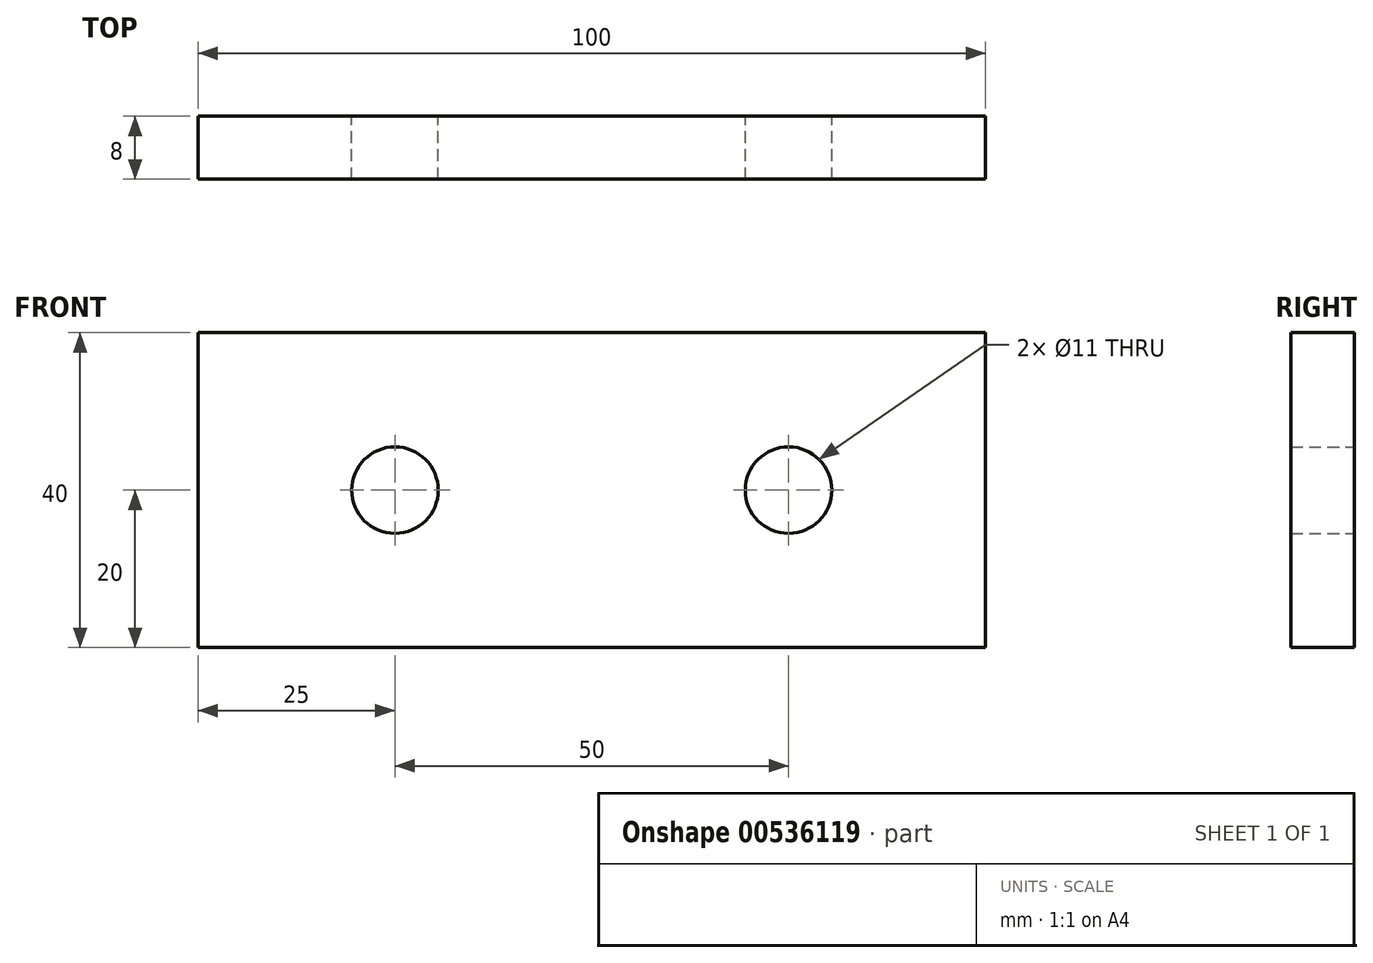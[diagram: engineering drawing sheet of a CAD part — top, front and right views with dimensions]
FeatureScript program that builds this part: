
annotation { "Feature Type Name" : "Feature", "Feature Type Description" : "" }
export const myFeature = defineFeature(function(context is Context, id is Id, definition is map)
    precondition{}
    {
        {
            var Q0;
            Q0=qCreatedBy(makeId("Front.planeOp"),FACE);
            var sketch = newSketch(context, id + "F0", { "sketchPlane" : qUnion([Q0])});
            skLineSegment(sketch, "E0.bottom", {"start": v(50, 20) * mm, "end": v(-50, 20) * mm});
            skLineSegment(sketch, "E0.top", {"start": v(50, -20) * mm, "end": v(-50, -20) * mm});
            skLineSegment(sketch, "E0.left", {"start": v(50, 20) * mm, "end": v(50, -20) * mm});
            skLineSegment(sketch, "E0.right", {"start": v(-50, 20) * mm, "end": v(-50, -20) * mm});
            skPoint(sketch, "E0.middle", {"position": v(0, 0) * mm});
            skCircle(sketch, "E1", {"center": v(-25, 0) * mm, "radius": 5 * mm});
            skCircle(sketch, "E2", {"center": v(25, 0) * mm, "radius": 5 * mm});
            skSolve(sketch);
        }
        {
            var Q0;
            Q0=makeQuery(id+"F0.imprint","IMPRINT",FACE,{"disambiguationData":[TD([[makeQuery(id+"F0.imprint","IMPRINT",EDGE,{"derivedFrom":sQuery(id+"F0.wireOp",EDGE,"E0.bottom")}),1.0]])]});
            var Q1;
            Q1=makeQuery(id+"F0.imprint","IMPRINT",FACE,{"disambiguationData":[TD([[makeQuery(id+"F0.imprint","IMPRINT",EDGE,{"derivedFrom":sQuery(id+"F0.wireOp",EDGE,"E1")}),1.0]])]});
            var Q2;
            Q2=makeQuery(id+"F0.imprint","IMPRINT",FACE,{"disambiguationData":[TD([[makeQuery(id+"F0.imprint","IMPRINT",EDGE,{"derivedFrom":sQuery(id+"F0.wireOp",EDGE,"E2")}),1.0]])]});
            extrude(context, id + "F1", {"entities" : qUnion([Q0, Q1, Q2]), "depth" : 8 * mm, "offsetDistance" : 25 * mm});
        }
        {
            var Q0;
            Q0=sQuery(id+"F0.wireOp",VERTEX,"E1.center");
            var Q1;
            Q1=sQuery(id+"F0.wireOp",VERTEX,"E2.center");
            var Q2;
            Q2=makeQuery(id+"F1.opExtrude","SWEPT_BODY",BODY,{"disambiguationData":[OSD([sQuery(id+"F0.wireOp",EDGE,"E0.bottom"),sQuery(id+"F0.wireOp",EDGE,"E0.top"),sQuery(id+"F0.wireOp",EDGE,"E0.left"),sQuery(id+"F0.wireOp",EDGE,"E0.right")])]});
            hole(context, id + "F2", {"style" : HoleStyle.SIMPLE, "endStyle" : HoleEndStyle.THROUGH, "oppositeDirection" : true, "standardTappedOrClearance" : lookupTablePath({ "standard" : "ISO", "fit" : "Normal", "size" : "M10", "type" : "Clearance" }), "standardBlindInLast" : lookupTablePath({ "fit" : "Standard", "standard" : "ISO", "size" : "M10", "type" : "Clearance" }), "holeDiameter" : 11 * mm, "isTappedThrough" : true, "tappedDepth" : 12 * mm, "tapClearance" : 3, "locations" : qUnion([Q0, Q1]), "scope" : qUnion([Q2])});
        }
    });
